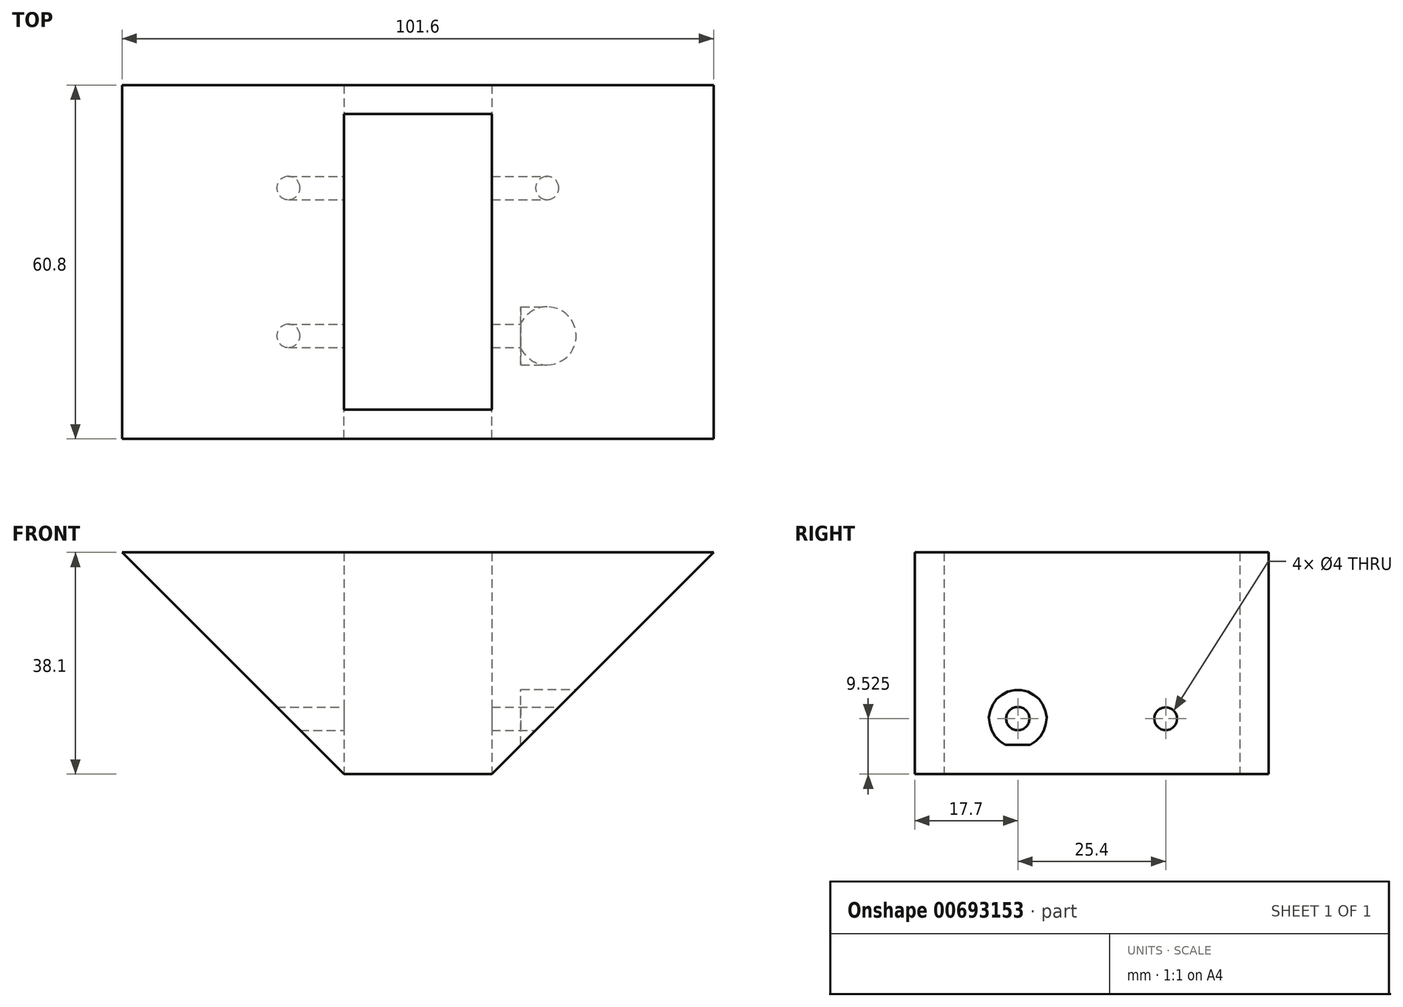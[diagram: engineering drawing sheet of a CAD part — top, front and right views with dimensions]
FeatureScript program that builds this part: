
annotation { "Feature Type Name" : "Feature", "Feature Type Description" : "" }
export const myFeature = defineFeature(function(context is Context, id is Id, definition is map)
    precondition{}
    {
        {
            var Q0;
            Q0=qCreatedBy(makeId("Front.planeOp"),FACE);
            var sketch = newSketch(context, id + "F0", { "sketchPlane" : qUnion([Q0])});
            skLineSegment(sketch, "E0.bottom", {"start": v(12.7, 63.5) * mm, "end": v(-12.7, 63.5) * mm, "construction": true});
            skLineSegment(sketch, "E0.top", {"start": v(12.7, -63.5) * mm, "end": v(-12.7, -63.5) * mm, "construction": true});
            skLineSegment(sketch, "E0.left", {"start": v(12.7, 63.5) * mm, "end": v(12.7, -63.5) * mm, "construction": true});
            skLineSegment(sketch, "E0.right", {"start": v(-12.7, 63.5) * mm, "end": v(-12.7, -63.5) * mm, "construction": true});
            skPoint(sketch, "E0.middle", {"position": v(0, 0) * mm});
            skLineSegment(sketch, "E1.bottom", {"start": v(-127, 88.9) * mm, "end": v(127, 88.9) * mm, "construction": true});
            skLineSegment(sketch, "E1.top", {"start": v(-127, 63.5) * mm, "end": v(127, 63.5) * mm, "construction": true});
            skLineSegment(sketch, "E1.left", {"start": v(-127, 88.9) * mm, "end": v(-127, 63.5) * mm, "construction": true});
            skLineSegment(sketch, "E1.right", {"start": v(127, 88.9) * mm, "end": v(127, 63.5) * mm, "construction": true});
            skLineSegment(sketch, "E2", {"start": v(0, -63.5) * mm, "end": v(0, 88.9) * mm, "construction": true});
            skLineSegment(sketch, "E3", {"start": v(-50.8, 63.5) * mm, "end": v(-12.7, 25.4) * mm});
            skLineSegment(sketch, "E4", {"start": v(-12.7, 25.4) * mm, "end": v(12.7, 25.4) * mm});
            skLineSegment(sketch, "E5", {"start": v(12.7, 25.4) * mm, "end": v(50.8, 63.5) * mm});
            skLineSegment(sketch, "E6", {"start": v(50.8, 63.5) * mm, "end": v(12.7, 63.5) * mm});
            skLineSegment(sketch, "E7", {"start": v(-50.8, 63.5) * mm, "end": v(-12.7, 63.5) * mm});
            skLineSegment(sketch, "E8", {"start": v(-12.7, 63.5) * mm, "end": v(-12.7, 25.4) * mm});
            skLineSegment(sketch, "E9", {"start": v(12.7, 63.5) * mm, "end": v(12.7, 25.4) * mm});
            skLineSegment(sketch, "E10", {"start": v(-12.7, 63.5) * mm, "end": v(12.7, 63.5) * mm});
            skSolve(sketch);
        }
        {
            var Q0;
            Q0 = qSketchRegion(id + "F0", true);
            extrude(context, id + "F1", {"entities" : qUnion([Q0]), "depth" : 5 * mm, "offsetDistance" : 25.4 * mm});
        }
        {
            var Q0;
            Q0=makeQuery(id+"F0.imprint","IMPRINT",FACE,{"disambiguationData":[TD([[makeQuery(id+"F0.imprint","IMPRINT",EDGE,{"derivedFrom":sQuery(id+"F0.wireOp",EDGE,"E5")}),1.0]])]});
            var Q1;
            Q1=makeQuery(id+"F0.imprint","IMPRINT",FACE,{"disambiguationData":[TD([[makeQuery(id+"F0.imprint","IMPRINT",EDGE,{"derivedFrom":sQuery(id+"F0.wireOp",EDGE,"E3")}),1.0]])]});
            extrude(context, id + "F2", {"entities" : qUnion([Q0, Q1]), "operationType" : NewBodyOperationType.ADD, "oppositeDirection" : true, "depth" : 50.8 * mm, "offsetDistance" : 25.4 * mm});
        }
        {
            var Q0;
            Q0=makeQuery(id+"F2.opExtrude","CAP_FACE",FACE,{"disambiguationData":[OSD([sQuery(id+"F0.wireOp",EDGE,"E5"),sQuery(id+"F0.wireOp",EDGE,"E6"),sQuery(id+"F0.wireOp",EDGE,"E9")])],"isStart":false});
            var sketch = newSketch(context, id + "F3", { "sketchPlane" : qUnion([Q0])});
            skLineSegment(sketch, "E11.0.0", {"start": v(12.7, 63.5) * mm, "end": v(12.7, 25.4) * mm});
            skLineSegment(sketch, "E11.0.1", {"start": v(12.7, 25.4) * mm, "end": v(50.8, 63.5) * mm});
            skLineSegment(sketch, "E11.0.2", {"start": v(50.8, 63.5) * mm, "end": v(12.7, 63.5) * mm});
            skLineSegment(sketch, "E12", {"start": v(-12.7, 63.5) * mm, "end": v(-50.8, 63.5) * mm});
            skLineSegment(sketch, "E13", {"start": v(-50.8, 63.5) * mm, "end": v(-12.7, 25.4) * mm});
            skLineSegment(sketch, "E14", {"start": v(-12.7, 25.4) * mm, "end": v(-12.7, 63.5) * mm});
            skLineSegment(sketch, "E15", {"start": v(-12.7, 63.5) * mm, "end": v(12.7, 63.5) * mm});
            skLineSegment(sketch, "E16", {"start": v(12.7, 25.4) * mm, "end": v(-12.7, 25.4) * mm});
            skSolve(sketch);
        }
        {
            var Q0;
            Q0 = qSketchRegion(id + "F3", true);
            extrude(context, id + "F4", {"entities" : qUnion([Q0]), "operationType" : NewBodyOperationType.ADD, "depth" : 5 * mm, "offsetDistance" : 25.4 * mm});
        }
        {
            var Q0;
            Q0=qCreatedBy(makeId("Right.planeOp"),FACE);
            var sketch = newSketch(context, id + "F5", { "sketchPlane" : qUnion([Q0])});
            skLineSegment(sketch, "E17.0", {"start": v(-5, 63.5) * mm, "end": v(55.8, 63.5) * mm, "construction": true});
            skLineSegment(sketch, "E18.0", {"start": v(-5, 25.4) * mm, "end": v(-5, 63.5) * mm, "construction": true});
            skLineSegment(sketch, "E18.1", {"start": v(55.8, 25.4) * mm, "end": v(55.8, 63.5) * mm, "construction": true});
            skLineSegment(sketch, "E19.0", {"start": v(50.8, 63.5) * mm, "end": v(50.8, 25.4) * mm, "construction": true});
            skLineSegment(sketch, "E19.1", {"start": v(0, 63.5) * mm, "end": v(0, 25.4) * mm, "construction": true});
            skLineSegment(sketch, "E20.0", {"start": v(50.8, 25.4) * mm, "end": v(0, 25.4) * mm, "construction": true});
            skLineSegment(sketch, "E21", {"start": v(12.7, 25.4) * mm, "end": v(12.7, 63.5) * mm, "construction": true});
            skLineSegment(sketch, "E22", {"start": v(38.1, 63.5) * mm, "end": v(38.1, 25.4) * mm, "construction": true});
            skLineSegment(sketch, "E23", {"start": v(-5, 44.45) * mm, "end": v(55.8, 44.45) * mm, "construction": true});
            skLineSegment(sketch, "E24", {"start": v(25.4, 44.45) * mm, "end": v(25.4, 25.4) * mm, "construction": true});
            skLineSegment(sketch, "E25", {"start": v(25.4, 34.93) * mm, "end": v(55.8, 34.93) * mm, "construction": true});
            skCircle(sketch, "E26", {"center": v(38.1, 34.93) * mm, "radius": 2 * mm});
            skCircle(sketch, "E27.MirrorC", {"center": v(12.7, 34.93) * mm, "radius": 2 * mm});
            skCircle(sketch, "E28", {"center": v(12.7, 34.93) * mm, "radius": 5 * mm, "construction": true});
            skSolve(sketch);
        }
        {
            var Q0;
            Q0 = qSketchRegion(id + "F5", true);
            extrude(context, id + "F6", {"entities" : qUnion([Q0]), "operationType" : NewBodyOperationType.REMOVE, "endBound" : BoundingType.THROUGH_ALL, "oppositeDirection" : true, "depth" : 25.4 * mm, "offsetDistance" : 25.4 * mm, "hasSecondDirection" : true, "secondDirectionBound" : SecondDirectionBoundingType.THROUGH_ALL, "secondDirectionOppositeDirection" : false, "secondDirectionDepth" : 25.4 * mm});
        }
        {
            var Q0;
            Q0=qCreatedBy(makeId("Right.planeOp"),FACE);
            cPlane(context, id + "F7", {"entities" : qUnion([Q0]), "cplaneType" : CPlaneType.OFFSET, "offset" : 50.8 * mm, "width" : 152.4 * mm, "height" : 152.4 * mm});
        }
        {
            var Q0;
            Q0=qCreatedBy(id+"F7.planeOp",FACE);
            var sketch = newSketch(context, id + "F8", { "sketchPlane" : qUnion([Q0])});
            skCircle(sketch, "E29.0", {"center": v(12.7, 34.93) * mm, "radius": 5 * mm});
            skLineSegment(sketch, "E30.0", {"start": v(25.4, 44.45) * mm, "end": v(25.4, 25.4) * mm, "construction": true});
            skCircle(sketch, "E31.MirrorC", {"center": v(38.1, 34.93) * mm, "radius": 5 * mm});
            skSolve(sketch);
        }
        {
            var Q0;
            Q0=makeQuery(id+"F8.imprint","IMPRINT",FACE,{"disambiguationData":[TD([[makeQuery(id+"F8.imprint","IMPRINT",EDGE,{"derivedFrom":sQuery(id+"F8.wireOp",EDGE,"E31.MirrorC")}),-1.0]])]});
            var Q1;
            Q1=makeQuery(id+"F8.imprint","IMPRINT",FACE,{"disambiguationData":[TD([[makeQuery(id+"F8.imprint","IMPRINT",EDGE,{"derivedFrom":sQuery(id+"F8.wireOp",EDGE,"E29.0")}),1.0]])]});
            var Q2;
            Q2=makeQuery(id+"F2.opExtrude","SWEPT_FACE",FACE,{"disambiguationData":[OSD([sQuery(id+"F0.wireOp",EDGE,"E9")])]});
            extrude(context, id + "F9", {"entities" : qUnion([Q0, Q1]), "operationType" : NewBodyOperationType.REMOVE, "endBound" : BoundingType.UP_TO_SURFACE, "oppositeDirection" : true, "depth" : 25.4 * mm, "endBoundEntityFace" : qUnion([Q2]), "hasOffset" : true, "offsetDistance" : 5 * mm});
        }
    });
